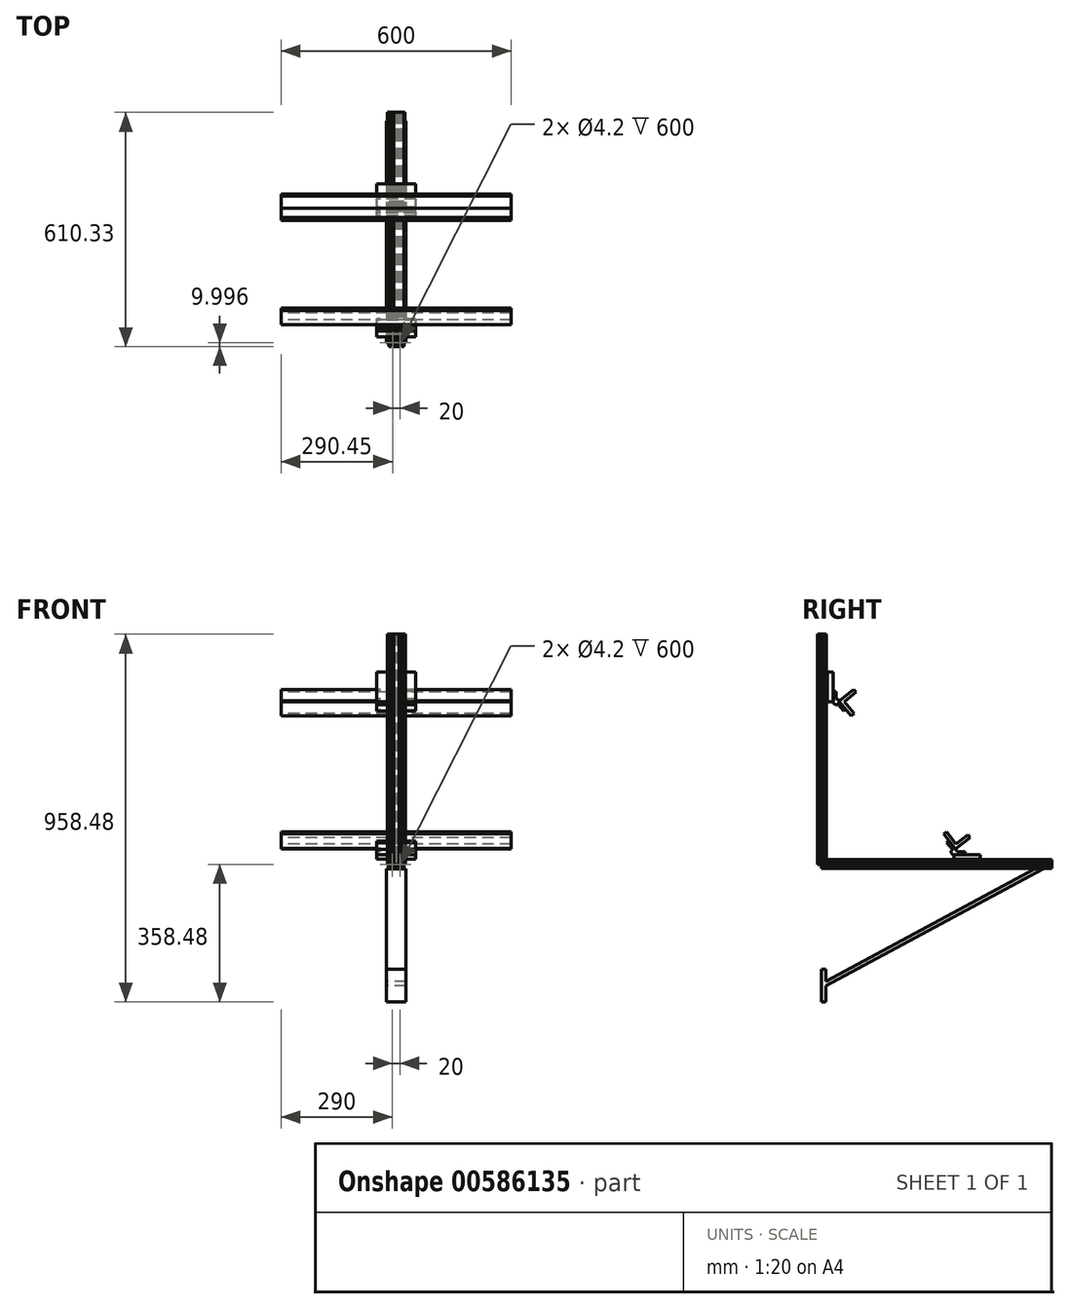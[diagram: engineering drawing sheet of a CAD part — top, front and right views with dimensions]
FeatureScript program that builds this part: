
annotation { "Feature Type Name" : "Feature", "Feature Type Description" : "" }
export const myFeature = defineFeature(function(context is Context, id is Id, definition is map)
    precondition{}
    {
        {
            var Q0;
            Q0=qCreatedBy(makeId("Front.planeOp"),FACE);
            var sketch = newSketch(context, id + "F0", { "sketchPlane" : qUnion([Q0])});
            skLineSegment(sketch, "E0.bottom", {"start": v(20, -10) * mm, "end": v(13, -10) * mm});
            skLineSegment(sketch, "E0.top", {"start": v(20, 10) * mm, "end": v(-7, 10) * mm});
            skLineSegment(sketch, "E0.left", {"start": v(20, -10) * mm, "end": v(20, -3) * mm});
            skLineSegment(sketch, "E0.right", {"start": v(-20, -10) * mm, "end": v(-20, -3) * mm});
            skPoint(sketch, "E0.middle", {"position": v(0, 0) * mm});
            skLineSegment(sketch, "E1.bottom", {"start": v(-8, -3) * mm, "end": v(-12, -3) * mm});
            skLineSegment(sketch, "E1.top", {"start": v(-8, 3) * mm, "end": v(-12, 3) * mm});
            skLineSegment(sketch, "E1.left", {"start": v(-7, -2) * mm, "end": v(-7, 2) * mm});
            skLineSegment(sketch, "E1.right", {"start": v(-13, -2) * mm, "end": v(-13, 2) * mm});
            skPoint(sketch, "E1.middle", {"position": v(-10, 0) * mm});
            skLineSegment(sketch, "E2.bottom", {"start": v(8, -3) * mm, "end": v(12, -3) * mm});
            skLineSegment(sketch, "E2.top", {"start": v(8, 3) * mm, "end": v(12, 3) * mm});
            skLineSegment(sketch, "E2.left", {"start": v(7, -2) * mm, "end": v(7, 2) * mm});
            skLineSegment(sketch, "E2.right", {"start": v(13, -2) * mm, "end": v(13, 2) * mm});
            skPoint(sketch, "E2.middle", {"position": v(10, 0) * mm});
            skLineSegment(sketch, "E3.bottom", {"start": v(-3, -8) * mm, "end": v(-7, -8) * mm});
            skLineSegment(sketch, "E3.top", {"start": v(-3, 8) * mm, "end": v(-7, 8) * mm});
            skLineSegment(sketch, "E3.right", {"start": v(-18, -6) * mm, "end": v(-18, -3) * mm});
            skLineSegment(sketch, "E4.bottom", {"start": v(3, -8) * mm, "end": v(7, -8) * mm});
            skLineSegment(sketch, "E4.top", {"start": v(3, 8) * mm, "end": v(16, 8) * mm});
            skLineSegment(sketch, "E5.bottom", {"start": v(-20, 10) * mm, "end": v(-16, 10) * mm});
            skLineSegment(sketch, "E5.top", {"start": v(-18, 6) * mm, "end": v(-17, 6) * mm});
            skLineSegment(sketch, "E5.right", {"start": v(-16, 8) * mm, "end": v(-16, 7) * mm});
            skPoint(sketch, "E5.middle", {"position": v(-18, 8) * mm});
            skLineSegment(sketch, "E6.bottom", {"start": v(-20, 10) * mm, "end": v(-19, 10) * mm});
            skLineSegment(sketch, "E7.top", {"start": v(-1, -10) * mm, "end": v(0, -10) * mm});
            skLineSegment(sketch, "E8", {"start": v(-16, 7) * mm, "end": v(-12, 3) * mm});
            skLineSegment(sketch, "E9", {"start": v(-3, -8) * mm, "end": v(-8, -3) * mm});
            skLineSegment(sketch, "E10.MirrorCS", {"start": v(-16, -7) * mm, "end": v(-12, -3) * mm});
            skLineSegment(sketch, "E11.MirrorCS", {"start": v(-3, 8) * mm, "end": v(-8, 3) * mm});
            skLineSegment(sketch, "E12.MirrorCS", {"start": v(3, 8) * mm, "end": v(8, 3) * mm});
            skLineSegment(sketch, "E13.MirrorCS", {"start": v(16, -7) * mm, "end": v(12, -3) * mm});
            skLineSegment(sketch, "E14.MirrorCS", {"start": v(16, 7) * mm, "end": v(12, 3) * mm});
            skLineSegment(sketch, "E15.MirrorCS", {"start": v(3, -8) * mm, "end": v(8, -3) * mm});
            skLineSegment(sketch, "E16.bottom", {"start": v(20, 10) * mm, "end": v(16, 10) * mm});
            skLineSegment(sketch, "E16.top", {"start": v(18, 6) * mm, "end": v(17, 6) * mm});
            skLineSegment(sketch, "E16.right", {"start": v(16, 8) * mm, "end": v(16, 7) * mm});
            skPoint(sketch, "E16.middle", {"position": v(18, 8) * mm});
            skLineSegment(sketch, "E17.bottom", {"start": v(20, -10) * mm, "end": v(16, -10) * mm});
            skLineSegment(sketch, "E17.top", {"start": v(18, -6) * mm, "end": v(17, -6) * mm});
            skLineSegment(sketch, "E17.left", {"start": v(20, -10) * mm, "end": v(20, -6) * mm});
            skLineSegment(sketch, "E17.right", {"start": v(16, -8) * mm, "end": v(16, -7) * mm});
            skPoint(sketch, "E17.middle", {"position": v(18, -8) * mm});
            skPoint(sketch, "E18.orphan", {"position": v(19, 10) * mm});
            skPoint(sketch, "E19.orphan", {"position": v(20, 9) * mm});
            skPoint(sketch, "E20.orphan", {"position": v(16, 6) * mm});
            skPoint(sketch, "E21.orphan", {"position": v(13, 3) * mm});
            skLineSegment(sketch, "E22.trimOffspring", {"start": v(13, -2) * mm, "end": v(17, -6) * mm});
            skLineSegment(sketch, "E23.trimOffspring", {"start": v(7, 2) * mm, "end": v(2, 7) * mm});
            skLineSegment(sketch, "E24.trimOffspring", {"start": v(7, -2) * mm, "end": v(2, -7) * mm});
            skLineSegment(sketch, "E25.trimOffspring", {"start": v(13, 2) * mm, "end": v(17, 6) * mm});
            skPoint(sketch, "E26.orphan", {"position": v(13, -3) * mm});
            skPoint(sketch, "E27.orphan", {"position": v(7, 3) * mm});
            skPoint(sketch, "E28.orphan", {"position": v(7, -3) * mm});
            skPoint(sketch, "E29.orphan", {"position": v(16, -6) * mm});
            skLineSegment(sketch, "E30.trimOffspring", {"start": v(18, -6) * mm, "end": v(18, -3) * mm});
            skPoint(sketch, "E31.trimOffspring.end.orphan", {"position": v(20, -9) * mm});
            skPoint(sketch, "E32.orphan", {"position": v(19, -10) * mm});
            skPoint(sketch, "E7.left.start.orphan", {"position": v(-1, -9) * mm});
            skPoint(sketch, "E33.orphan", {"position": v(-2, -8) * mm});
            skPoint(sketch, "E34.orphan", {"position": v(-18, -8) * mm});
            skPoint(sketch, "E35.orphan", {"position": v(-19, -10) * mm});
            skPoint(sketch, "E36.orphan", {"position": v(-20, -9) * mm});
            skPoint(sketch, "E37.orphan", {"position": v(-16, 6) * mm});
            skPoint(sketch, "E38.orphan", {"position": v(-1, 10) * mm});
            skPoint(sketch, "E39.orphan", {"position": v(0, 9) * mm});
            skPoint(sketch, "E40.orphan", {"position": v(1, 10) * mm});
            skPoint(sketch, "E41.orphan", {"position": v(2, 8) * mm});
            skPoint(sketch, "E42.orphan", {"position": v(-2, 8) * mm});
            skPoint(sketch, "E43.orphan", {"position": v(0, -9) * mm});
            skPoint(sketch, "E44.orphan", {"position": v(1, -10) * mm});
            skPoint(sketch, "E45.orphan", {"position": v(2, -8) * mm});
            skLineSegment(sketch, "E46", {"start": v(-1, -8) * mm, "end": v(1, -8) * mm});
            skLineSegment(sketch, "E47", {"start": v(1, 8) * mm, "end": v(-1, 8) * mm});
            skLineSegment(sketch, "E48", {"start": v(-2, 7) * mm, "end": v(-1, 8) * mm});
            skLineSegment(sketch, "E49", {"start": v(2, 7) * mm, "end": v(1, 8) * mm});
            skLineSegment(sketch, "E50", {"start": v(-2, -7) * mm, "end": v(-1, -8) * mm});
            skLineSegment(sketch, "E51", {"start": v(2, -7) * mm, "end": v(1, -8) * mm});
            skPoint(sketch, "E52.orphan", {"position": v(-13, 3) * mm});
            skPoint(sketch, "E53.orphan", {"position": v(-7, 3) * mm});
            skPoint(sketch, "E54.orphan", {"position": v(-7, -3) * mm});
            skPoint(sketch, "E55.orphan", {"position": v(-13, -3) * mm});
            skLineSegment(sketch, "E56.trimOffspring", {"start": v(-13, 2) * mm, "end": v(-17, 6) * mm});
            skLineSegment(sketch, "E57.trimOffspring", {"start": v(-7, -2) * mm, "end": v(-2, -7) * mm});
            skLineSegment(sketch, "E58.trimOffspring", {"start": v(-7, 2) * mm, "end": v(-2, 7) * mm});
            skLineSegment(sketch, "E59.trimOffspring", {"start": v(-13, -2) * mm, "end": v(-17, -6) * mm});
            skLineSegment(sketch, "E60.bottom", {"start": v(-20, -10) * mm, "end": v(-16, -10) * mm});
            skLineSegment(sketch, "E60.top", {"start": v(-18, -6) * mm, "end": v(-17, -6) * mm});
            skLineSegment(sketch, "E60.left", {"start": v(-20, -10) * mm, "end": v(-20, -6) * mm});
            skLineSegment(sketch, "E60.right", {"start": v(-16, -8) * mm, "end": v(-16, -7) * mm});
            skPoint(sketch, "E61.orphan", {"position": v(-16, -6) * mm});
            skLineSegment(sketch, "E62", {"start": v(-13, -8) * mm, "end": v(-13, -10) * mm});
            skLineSegment(sketch, "E63", {"start": v(-7, -8) * mm, "end": v(-7, -10) * mm});
            skLineSegment(sketch, "E64", {"start": v(-18, 3) * mm, "end": v(-20, 3) * mm});
            skLineSegment(sketch, "E65", {"start": v(-18, -3) * mm, "end": v(-20, -3) * mm});
            skLineSegment(sketch, "E66", {"start": v(-13, 8) * mm, "end": v(-13, 10) * mm});
            skLineSegment(sketch, "E67", {"start": v(-7, 8) * mm, "end": v(-7, 10) * mm});
            skLineSegment(sketch, "E68.MirrorCS", {"start": v(18, 3) * mm, "end": v(20, 3) * mm});
            skLineSegment(sketch, "E69.MirrorCS", {"start": v(18, -3) * mm, "end": v(20, -3) * mm});
            skLineSegment(sketch, "E70.MirrorCS", {"start": v(13, -8) * mm, "end": v(13, -10) * mm});
            skLineSegment(sketch, "E71.MirrorCS", {"start": v(7, -8) * mm, "end": v(7, -10) * mm});
            skLineSegment(sketch, "E72.trimOffspring", {"start": v(-18, 3) * mm, "end": v(-18, 6) * mm});
            skLineSegment(sketch, "E73.trimOffspring", {"start": v(-20, 3) * mm, "end": v(-20, 7.62) * mm});
            skLineSegment(sketch, "E74.trimOffspring", {"start": v(-13, 10) * mm, "end": v(-20, 10) * mm});
            skLineSegment(sketch, "E75.trimOffspring", {"start": v(-13, 8) * mm, "end": v(-16, 8) * mm});
            skLineSegment(sketch, "E76.trimOffspring", {"start": v(-13, -8) * mm, "end": v(-16, -8) * mm});
            skLineSegment(sketch, "E77.trimOffspring", {"start": v(-13, -10) * mm, "end": v(-20, -10) * mm});
            skLineSegment(sketch, "E78.trimOffspring", {"start": v(13, -8) * mm, "end": v(16, -8) * mm});
            skLineSegment(sketch, "E79.trimOffspring", {"start": v(7, -10) * mm, "end": v(-7, -10) * mm});
            skLineSegment(sketch, "E80.trimOffspring", {"start": v(20, 3) * mm, "end": v(20, 6) * mm});
            skLineSegment(sketch, "E81.trimOffspring", {"start": v(18, 3) * mm, "end": v(18, 6) * mm});
            skCircle(sketch, "E82", {"center": v(-10, 0) * mm, "radius": 2.1 * mm});
            skCircle(sketch, "E83.MirrorC", {"center": v(10, 0) * mm, "radius": 2.1 * mm});
            skLineSegment(sketch, "E84.top", {"start": v(20, 12.38) * mm, "end": v(20.44, 12.38) * mm});
            skLineSegment(sketch, "E84.left", {"start": v(20, 10) * mm, "end": v(20, 12.38) * mm});
            skLineSegment(sketch, "E85", {"start": v(20.44, 12.38) * mm, "end": v(23.18, 10) * mm});
            skLineSegment(sketch, "E86.MirrorCS", {"start": v(20.44, 7.62) * mm, "end": v(23.18, 10) * mm});
            skLineSegment(sketch, "E87.MirrorCS", {"start": v(20, 7.62) * mm, "end": v(20.44, 7.62) * mm});
            skLineSegment(sketch, "E88.MirrorCS", {"start": v(-20, 7.62) * mm, "end": v(-20.44, 7.62) * mm});
            skLineSegment(sketch, "E89.MirrorCS", {"start": v(-20.44, 7.62) * mm, "end": v(-23.18, 10) * mm});
            skLineSegment(sketch, "E90.MirrorCS", {"start": v(-20.44, 12.38) * mm, "end": v(-23.18, 10) * mm});
            skLineSegment(sketch, "E91.MirrorCS", {"start": v(-20, 12.38) * mm, "end": v(-20.44, 12.38) * mm});
            skLineSegment(sketch, "E92.MirrorCS", {"start": v(-20, 10) * mm, "end": v(-20, 12.38) * mm});
            skLineSegment(sketch, "E93.trimOffspring", {"start": v(-20, 7.62) * mm, "end": v(-20, 6) * mm});
            skPoint(sketch, "E94.trimOffspring.start.orphan", {"position": v(-20, 9) * mm});
            skLineSegment(sketch, "E95.trimOffspring", {"start": v(20, 7.62) * mm, "end": v(20, 6) * mm});
            skSolve(sketch);
        }
        {
            var Q0;
            Q0 = qSketchRegion(id + "F0", true);
            extrude(context, id + "F1", {"entities" : qUnion([Q0]), "oppositeDirection" : true, "depth" : 600 * mm, "offsetDistance" : 25.4 * mm});
        }
        {
            var Q0;
            Q0=qCreatedBy(makeId("Top.planeOp"),FACE);
            var sketch = newSketch(context, id + "F2", { "sketchPlane" : qUnion([Q0])});
            skLineSegment(sketch, "E96.bottom", {"start": v(20.45, -10.33) * mm, "end": v(13.45, -10.33) * mm});
            skLineSegment(sketch, "E96.top", {"start": v(20.45, 9.67) * mm, "end": v(-6.55, 9.67) * mm});
            skLineSegment(sketch, "E96.left", {"start": v(20.45, -10.33) * mm, "end": v(20.45, -3.33) * mm});
            skLineSegment(sketch, "E96.right", {"start": v(-19.55, -10.33) * mm, "end": v(-19.55, -3.33) * mm});
            skPoint(sketch, "E96.middle", {"position": v(0.45, -0.33) * mm});
            skLineSegment(sketch, "E97.bottom", {"start": v(-7.55, -3.33) * mm, "end": v(-11.55, -3.33) * mm});
            skLineSegment(sketch, "E97.top", {"start": v(-7.55, 2.67) * mm, "end": v(-11.55, 2.67) * mm});
            skLineSegment(sketch, "E97.left", {"start": v(-6.55, -2.33) * mm, "end": v(-6.55, 1.67) * mm});
            skLineSegment(sketch, "E97.right", {"start": v(-12.55, -2.33) * mm, "end": v(-12.55, 1.67) * mm});
            skPoint(sketch, "E97.middle", {"position": v(-9.55, -0.33) * mm});
            skLineSegment(sketch, "E98.bottom", {"start": v(8.45, -3.33) * mm, "end": v(12.45, -3.33) * mm});
            skLineSegment(sketch, "E98.top", {"start": v(8.45, 2.67) * mm, "end": v(12.45, 2.67) * mm});
            skLineSegment(sketch, "E98.left", {"start": v(7.45, -2.33) * mm, "end": v(7.45, 1.67) * mm});
            skLineSegment(sketch, "E98.right", {"start": v(13.45, -2.33) * mm, "end": v(13.45, 1.67) * mm});
            skPoint(sketch, "E98.middle", {"position": v(10.45, -0.33) * mm});
            skLineSegment(sketch, "E99.bottom", {"start": v(-2.55, -8.33) * mm, "end": v(-6.55, -8.33) * mm});
            skLineSegment(sketch, "E99.top", {"start": v(-2.55, 7.67) * mm, "end": v(-6.55, 7.67) * mm});
            skLineSegment(sketch, "E99.right", {"start": v(-17.55, -6.33) * mm, "end": v(-17.55, -3.33) * mm});
            skLineSegment(sketch, "E100.bottom", {"start": v(3.45, -8.33) * mm, "end": v(7.45, -8.33) * mm});
            skLineSegment(sketch, "E100.top", {"start": v(3.45, 7.67) * mm, "end": v(16.45, 7.67) * mm});
            skLineSegment(sketch, "E101.bottom", {"start": v(-19.55, 9.67) * mm, "end": v(-15.55, 9.67) * mm});
            skLineSegment(sketch, "E101.top", {"start": v(-17.55, 5.67) * mm, "end": v(-16.55, 5.67) * mm});
            skLineSegment(sketch, "E101.right", {"start": v(-15.55, 7.67) * mm, "end": v(-15.55, 6.67) * mm});
            skPoint(sketch, "E101.middle", {"position": v(-17.55, 7.67) * mm});
            skLineSegment(sketch, "E102.bottom", {"start": v(-19.55, 9.67) * mm, "end": v(-18.55, 9.67) * mm});
            skLineSegment(sketch, "E103.top", {"start": v(-0.55, -10.33) * mm, "end": v(0.45, -10.33) * mm});
            skLineSegment(sketch, "E104", {"start": v(-15.55, 6.67) * mm, "end": v(-11.55, 2.67) * mm});
            skLineSegment(sketch, "E105", {"start": v(-2.55, -8.33) * mm, "end": v(-7.55, -3.33) * mm});
            skLineSegment(sketch, "E106.MirrorCS", {"start": v(-15.55, -7.33) * mm, "end": v(-11.55, -3.33) * mm});
            skLineSegment(sketch, "E107.MirrorCS", {"start": v(-2.55, 7.67) * mm, "end": v(-7.55, 2.67) * mm});
            skLineSegment(sketch, "E108.MirrorCS", {"start": v(3.45, 7.67) * mm, "end": v(8.45, 2.67) * mm});
            skLineSegment(sketch, "E109.MirrorCS", {"start": v(16.45, -7.33) * mm, "end": v(12.45, -3.33) * mm});
            skLineSegment(sketch, "E110.MirrorCS", {"start": v(16.45, 6.67) * mm, "end": v(12.45, 2.67) * mm});
            skLineSegment(sketch, "E111.MirrorCS", {"start": v(3.45, -8.33) * mm, "end": v(8.45, -3.33) * mm});
            skLineSegment(sketch, "E112.bottom", {"start": v(20.45, 9.67) * mm, "end": v(16.45, 9.67) * mm});
            skLineSegment(sketch, "E112.top", {"start": v(18.45, 5.67) * mm, "end": v(17.45, 5.67) * mm});
            skLineSegment(sketch, "E112.right", {"start": v(16.45, 7.67) * mm, "end": v(16.45, 6.67) * mm});
            skPoint(sketch, "E112.middle", {"position": v(18.45, 7.67) * mm});
            skLineSegment(sketch, "E113.bottom", {"start": v(20.45, -10.33) * mm, "end": v(16.45, -10.33) * mm});
            skLineSegment(sketch, "E113.top", {"start": v(18.45, -6.33) * mm, "end": v(17.45, -6.33) * mm});
            skLineSegment(sketch, "E113.left", {"start": v(20.45, -10.33) * mm, "end": v(20.45, -6.33) * mm});
            skLineSegment(sketch, "E113.right", {"start": v(16.45, -8.33) * mm, "end": v(16.45, -7.33) * mm});
            skPoint(sketch, "E113.middle", {"position": v(18.45, -8.33) * mm});
            skPoint(sketch, "E114.orphan", {"position": v(19.45, 9.67) * mm});
            skPoint(sketch, "E115.orphan", {"position": v(20.45, 8.67) * mm});
            skPoint(sketch, "E116.orphan", {"position": v(16.45, 5.67) * mm});
            skPoint(sketch, "E117.orphan", {"position": v(13.45, 2.67) * mm});
            skLineSegment(sketch, "E118.trimOffspring", {"start": v(13.45, -2.33) * mm, "end": v(17.45, -6.33) * mm});
            skLineSegment(sketch, "E119.trimOffspring", {"start": v(7.45, 1.67) * mm, "end": v(2.45, 6.67) * mm});
            skLineSegment(sketch, "E120.trimOffspring", {"start": v(7.45, -2.33) * mm, "end": v(2.45, -7.33) * mm});
            skLineSegment(sketch, "E121.trimOffspring", {"start": v(13.45, 1.67) * mm, "end": v(17.45, 5.67) * mm});
            skPoint(sketch, "E122.orphan", {"position": v(13.45, -3.33) * mm});
            skPoint(sketch, "E123.orphan", {"position": v(7.45, 2.67) * mm});
            skPoint(sketch, "E124.orphan", {"position": v(7.45, -3.33) * mm});
            skPoint(sketch, "E125.orphan", {"position": v(16.45, -6.33) * mm});
            skLineSegment(sketch, "E126.trimOffspring", {"start": v(18.45, -6.33) * mm, "end": v(18.45, -3.33) * mm});
            skPoint(sketch, "E127.trimOffspring.end.orphan", {"position": v(20.45, -9.33) * mm});
            skPoint(sketch, "E128.orphan", {"position": v(19.45, -10.33) * mm});
            skPoint(sketch, "E103.left.start.orphan", {"position": v(-0.55, -9.33) * mm});
            skPoint(sketch, "E129.orphan", {"position": v(-1.55, -8.33) * mm});
            skPoint(sketch, "E130.orphan", {"position": v(-17.55, -8.33) * mm});
            skPoint(sketch, "E131.orphan", {"position": v(-18.55, -10.33) * mm});
            skPoint(sketch, "E132.orphan", {"position": v(-19.55, -9.33) * mm});
            skPoint(sketch, "E133.orphan", {"position": v(-15.55, 5.67) * mm});
            skPoint(sketch, "E134.orphan", {"position": v(-0.55, 9.67) * mm});
            skPoint(sketch, "E135.orphan", {"position": v(0.45, 8.67) * mm});
            skPoint(sketch, "E136.orphan", {"position": v(1.45, 9.67) * mm});
            skPoint(sketch, "E137.orphan", {"position": v(2.45, 7.67) * mm});
            skPoint(sketch, "E138.orphan", {"position": v(-1.55, 7.67) * mm});
            skPoint(sketch, "E139.orphan", {"position": v(0.45, -9.33) * mm});
            skPoint(sketch, "E140.orphan", {"position": v(1.45, -10.33) * mm});
            skPoint(sketch, "E141.orphan", {"position": v(2.45, -8.33) * mm});
            skLineSegment(sketch, "E142", {"start": v(-0.55, -8.33) * mm, "end": v(1.45, -8.33) * mm});
            skLineSegment(sketch, "E143", {"start": v(1.45, 7.67) * mm, "end": v(-0.55, 7.67) * mm});
            skLineSegment(sketch, "E144", {"start": v(-1.55, 6.67) * mm, "end": v(-0.55, 7.67) * mm});
            skLineSegment(sketch, "E145", {"start": v(2.45, 6.67) * mm, "end": v(1.45, 7.67) * mm});
            skLineSegment(sketch, "E146", {"start": v(-1.55, -7.33) * mm, "end": v(-0.55, -8.33) * mm});
            skLineSegment(sketch, "E147", {"start": v(2.45, -7.33) * mm, "end": v(1.45, -8.33) * mm});
            skPoint(sketch, "E148.orphan", {"position": v(-12.55, 2.67) * mm});
            skPoint(sketch, "E149.orphan", {"position": v(-6.55, 2.67) * mm});
            skPoint(sketch, "E150.orphan", {"position": v(-6.55, -3.33) * mm});
            skPoint(sketch, "E151.orphan", {"position": v(-12.55, -3.33) * mm});
            skLineSegment(sketch, "E152.trimOffspring", {"start": v(-12.55, 1.67) * mm, "end": v(-16.55, 5.67) * mm});
            skLineSegment(sketch, "E153.trimOffspring", {"start": v(-6.55, -2.33) * mm, "end": v(-1.55, -7.33) * mm});
            skLineSegment(sketch, "E154.trimOffspring", {"start": v(-6.55, 1.67) * mm, "end": v(-1.55, 6.67) * mm});
            skLineSegment(sketch, "E155.trimOffspring", {"start": v(-12.55, -2.33) * mm, "end": v(-16.55, -6.33) * mm});
            skLineSegment(sketch, "E156.bottom", {"start": v(-19.55, -10.33) * mm, "end": v(-15.55, -10.33) * mm});
            skLineSegment(sketch, "E156.top", {"start": v(-17.55, -6.33) * mm, "end": v(-16.55, -6.33) * mm});
            skLineSegment(sketch, "E156.left", {"start": v(-19.55, -10.33) * mm, "end": v(-19.55, -6.33) * mm});
            skLineSegment(sketch, "E156.right", {"start": v(-15.55, -8.33) * mm, "end": v(-15.55, -7.33) * mm});
            skPoint(sketch, "E157.orphan", {"position": v(-15.55, -6.33) * mm});
            skLineSegment(sketch, "E158", {"start": v(-12.55, -8.33) * mm, "end": v(-12.55, -10.33) * mm});
            skLineSegment(sketch, "E159", {"start": v(-6.55, -8.33) * mm, "end": v(-6.55, -10.33) * mm});
            skLineSegment(sketch, "E160", {"start": v(-17.55, 2.67) * mm, "end": v(-19.55, 2.67) * mm});
            skLineSegment(sketch, "E161", {"start": v(-17.55, -3.33) * mm, "end": v(-19.55, -3.33) * mm});
            skLineSegment(sketch, "E162", {"start": v(-12.55, 7.67) * mm, "end": v(-12.55, 9.67) * mm});
            skLineSegment(sketch, "E163", {"start": v(-6.55, 7.67) * mm, "end": v(-6.55, 9.67) * mm});
            skLineSegment(sketch, "E164.MirrorCS", {"start": v(18.45, 2.67) * mm, "end": v(20.45, 2.67) * mm});
            skLineSegment(sketch, "E165.MirrorCS", {"start": v(18.45, -3.33) * mm, "end": v(20.45, -3.33) * mm});
            skLineSegment(sketch, "E166.MirrorCS", {"start": v(13.45, -8.33) * mm, "end": v(13.45, -10.33) * mm});
            skLineSegment(sketch, "E167.MirrorCS", {"start": v(7.45, -8.33) * mm, "end": v(7.45, -10.33) * mm});
            skLineSegment(sketch, "E168.trimOffspring", {"start": v(-17.55, 2.67) * mm, "end": v(-17.55, 5.67) * mm});
            skLineSegment(sketch, "E169.trimOffspring", {"start": v(-19.55, 2.67) * mm, "end": v(-19.55, 7.29) * mm});
            skLineSegment(sketch, "E170.trimOffspring", {"start": v(-12.55, 9.67) * mm, "end": v(-19.55, 9.67) * mm});
            skLineSegment(sketch, "E171.trimOffspring", {"start": v(-12.55, 7.67) * mm, "end": v(-15.55, 7.67) * mm});
            skLineSegment(sketch, "E172.trimOffspring", {"start": v(-12.55, -8.33) * mm, "end": v(-15.55, -8.33) * mm});
            skLineSegment(sketch, "E173.trimOffspring", {"start": v(-12.55, -10.33) * mm, "end": v(-19.55, -10.33) * mm});
            skLineSegment(sketch, "E174.trimOffspring", {"start": v(13.45, -8.33) * mm, "end": v(16.45, -8.33) * mm});
            skLineSegment(sketch, "E175.trimOffspring", {"start": v(7.45, -10.33) * mm, "end": v(-6.55, -10.33) * mm});
            skLineSegment(sketch, "E176.trimOffspring", {"start": v(20.45, 2.67) * mm, "end": v(20.45, 5.67) * mm});
            skLineSegment(sketch, "E177.trimOffspring", {"start": v(18.45, 2.67) * mm, "end": v(18.45, 5.67) * mm});
            skCircle(sketch, "E178", {"center": v(-9.55, -0.33) * mm, "radius": 2.1 * mm});
            skCircle(sketch, "E179.MirrorC", {"center": v(10.45, -0.33) * mm, "radius": 2.1 * mm});
            skLineSegment(sketch, "E180.top", {"start": v(20.45, 12.05) * mm, "end": v(20.9, 12.05) * mm});
            skLineSegment(sketch, "E180.left", {"start": v(20.45, 9.67) * mm, "end": v(20.45, 12.05) * mm});
            skLineSegment(sketch, "E181", {"start": v(20.9, 12.05) * mm, "end": v(23.63, 9.67) * mm});
            skLineSegment(sketch, "E182.MirrorCS", {"start": v(20.9, 7.29) * mm, "end": v(23.63, 9.67) * mm});
            skLineSegment(sketch, "E183.MirrorCS", {"start": v(20.45, 7.29) * mm, "end": v(20.9, 7.29) * mm});
            skLineSegment(sketch, "E184.MirrorCS", {"start": v(-19.55, 7.29) * mm, "end": v(-20, 7.29) * mm});
            skLineSegment(sketch, "E185.MirrorCS", {"start": v(-20, 7.29) * mm, "end": v(-22.73, 9.67) * mm});
            skLineSegment(sketch, "E186.MirrorCS", {"start": v(-20, 12.05) * mm, "end": v(-22.73, 9.67) * mm});
            skLineSegment(sketch, "E187.MirrorCS", {"start": v(-19.55, 12.05) * mm, "end": v(-20, 12.05) * mm});
            skLineSegment(sketch, "E188.MirrorCS", {"start": v(-19.55, 9.67) * mm, "end": v(-19.55, 12.05) * mm});
            skLineSegment(sketch, "E189.trimOffspring", {"start": v(-19.55, 7.29) * mm, "end": v(-19.55, 5.67) * mm});
            skPoint(sketch, "E190.trimOffspring.start.orphan", {"position": v(-19.55, 8.67) * mm});
            skLineSegment(sketch, "E191.trimOffspring", {"start": v(20.45, 7.29) * mm, "end": v(20.45, 5.67) * mm});
            skSolve(sketch);
        }
        {
            var Q0;
            Q0 = qSketchRegion(id + "F2", true);
            extrude(context, id + "F3", {"entities" : qUnion([Q0]), "operationType" : NewBodyOperationType.ADD, "depth" : 600 * mm, "offsetDistance" : 25.4 * mm});
        }
        {
            var Q0;
            Q0=qCreatedBy(makeId("Right.planeOp"),FACE);
            var sketch = newSketch(context, id + "F4", { "sketchPlane" : qUnion([Q0])});
            skLineSegment(sketch, "E192.right", {"start": v(577.1, -11.57) * mm, "end": v(577.1, -11.74) * mm});
            skLineSegment(sketch, "E193", {"start": v(555.61, -11.57) * mm, "end": v(11.28, -304.62) * mm});
            skLineSegment(sketch, "E194", {"start": v(577.42, -11.57) * mm, "end": v(11.28, -316.37) * mm});
            skLineSegment(sketch, "E195", {"start": v(0, -322.44) * mm, "end": v(0, -310.7) * mm});
            skLineSegment(sketch, "E196", {"start": v(555.61, -11.57) * mm, "end": v(577.42, -11.57) * mm});
            skPoint(sketch, "E197.orphan", {"position": v(577.1, 0) * mm});
            skPoint(sketch, "E198.orphan", {"position": v(598.9, 0) * mm});
            skLineSegment(sketch, "E199.top", {"start": v(0, -358.48) * mm, "end": v(11.28, -358.48) * mm});
            skLineSegment(sketch, "E199.left", {"start": v(0, -291.08) * mm, "end": v(0, -358.48) * mm});
            skLineSegment(sketch, "E199.right", {"start": v(11.28, -291.08) * mm, "end": v(11.28, -304.62) * mm});
            skLineSegment(sketch, "E200.top", {"start": v(11.28, -272.73) * mm, "end": v(0, -272.73) * mm});
            skLineSegment(sketch, "E200.left", {"start": v(11.28, -291.08) * mm, "end": v(11.28, -272.73) * mm});
            skLineSegment(sketch, "E200.right", {"start": v(0, -291.08) * mm, "end": v(0, -272.73) * mm});
            skLineSegment(sketch, "E201.trimOffspring", {"start": v(11.28, -316.37) * mm, "end": v(11.28, -358.48) * mm});
            skSolve(sketch);
        }
        {
            var Q0;
            Q0 = qSketchRegion(id + "F4", true);
            extrude(context, id + "F5", {"entities" : qUnion([Q0]), "depth" : 25.4 * mm, "offsetDistance" : 25.4 * mm, "hasSecondDirection" : true, "secondDirectionOppositeDirection" : true, "secondDirectionDepth" : 25.4 * mm});
        }
        {
            var Q0;
            Q0=qCreatedBy(makeId("Right.planeOp"),FACE);
            var sketch = newSketch(context, id + "F6", { "sketchPlane" : qUnion([Q0])});
            skLineSegment(sketch, "E202", {"start": v(31.2, 420.16) * mm, "end": v(339.93, 26.86) * mm});
            skLineSegment(sketch, "E203.bottom", {"start": v(345.64, 13.63) * mm, "end": v(413.27, 13.63) * mm});
            skLineSegment(sketch, "E203.top", {"start": v(345.64, 25.03) * mm, "end": v(413.27, 25.03) * mm});
            skLineSegment(sketch, "E203.left", {"start": v(345.64, 13.63) * mm, "end": v(345.64, 25.03) * mm});
            skLineSegment(sketch, "E203.right", {"start": v(413.27, 13.63) * mm, "end": v(413.27, 25.03) * mm});
            skCircle(sketch, "E204", {"center": v(345.64, 32.7) * mm, "radius": 7.67 * mm});
            skLineSegment(sketch, "E205", {"start": v(345.64, 32.7) * mm, "end": v(326.32, 57.32) * mm});
            skLineSegment(sketch, "E206", {"start": v(326.32, 57.32) * mm, "end": v(330.53, 60.62) * mm});
            skLineSegment(sketch, "E207", {"start": v(330.53, 60.62) * mm, "end": v(346.46, 40.32) * mm});
            skLineSegment(sketch, "E208", {"start": v(185.56, 223.5) * mm, "end": v(222.86, 252.78) * mm});
            skLineSegment(sketch, "E209.MirrorCS", {"start": v(38.23, 424.32) * mm, "end": v(57.55, 399.7) * mm});
            skLineSegment(sketch, "E210.MirrorCS", {"start": v(57.55, 399.7) * mm, "end": v(61.76, 403.01) * mm});
            skLineSegment(sketch, "E211.MirrorCS", {"start": v(61.76, 403.01) * mm, "end": v(45.83, 423.3) * mm});
            skCircle(sketch, "E212.MirrorC", {"center": v(38.23, 424.32) * mm, "radius": 7.67 * mm});
            skLineSegment(sketch, "E213.bottom", {"start": v(30.56, 424.32) * mm, "end": v(15.48, 424.32) * mm});
            skLineSegment(sketch, "E213.top", {"start": v(30.56, 502) * mm, "end": v(15.48, 502) * mm});
            skLineSegment(sketch, "E213.left", {"start": v(30.56, 424.32) * mm, "end": v(30.56, 502) * mm});
            skLineSegment(sketch, "E213.right", {"start": v(15.48, 424.32) * mm, "end": v(15.48, 502) * mm});
            skLineSegment(sketch, "E214.bottom", {"start": v(38.23, 424.32) * mm, "end": v(38.23, 424.32) * mm});
            skLineSegment(sketch, "E214.top", {"start": v(38.23, 451.2) * mm, "end": v(38.23, 451.2) * mm});
            skLineSegment(sketch, "E214.left", {"start": v(38.23, 424.32) * mm, "end": v(38.23, 451.2) * mm});
            skLineSegment(sketch, "E214.right", {"start": v(38.23, 424.32) * mm, "end": v(38.23, 451.2) * mm});
            skLineSegment(sketch, "E215.right", {"start": v(30.56, 451.2) * mm, "end": v(30.56, 451.2) * mm});
            skLineSegment(sketch, "E216", {"start": v(345.64, 32.7) * mm, "end": v(374.18, 32.7) * mm});
            skLineSegment(sketch, "E217.bottom", {"start": v(38.23, 451.2) * mm, "end": v(30.95, 451.2) * mm});
            skLineSegment(sketch, "E217.top", {"start": v(38.23, 426.74) * mm, "end": v(30.95, 426.74) * mm});
            skLineSegment(sketch, "E217.left", {"start": v(38.23, 451.2) * mm, "end": v(38.23, 426.74) * mm});
            skLineSegment(sketch, "E217.right", {"start": v(30.95, 451.2) * mm, "end": v(30.95, 426.74) * mm});
            skLineSegment(sketch, "E218.bottom", {"start": v(374.18, 32.7) * mm, "end": v(347.68, 32.7) * mm});
            skLineSegment(sketch, "E218.top", {"start": v(374.18, 25.3) * mm, "end": v(347.68, 25.3) * mm});
            skLineSegment(sketch, "E218.left", {"start": v(374.18, 32.7) * mm, "end": v(374.18, 25.3) * mm});
            skLineSegment(sketch, "E218.right", {"start": v(347.68, 32.7) * mm, "end": v(347.68, 25.3) * mm});
            skSolve(sketch);
        }
        {
            var Q0;
            Q0 = qSketchRegion(id + "F6", true);
            extrude(context, id + "F7", {"entities" : qUnion([Q0]), "depth" : 50.8 * mm, "offsetDistance" : 25.4 * mm, "hasSecondDirection" : true, "secondDirectionOppositeDirection" : true, "secondDirectionDepth" : 50.8 * mm});
        }
        {
            var Q0;
            Q0=qCreatedBy(makeId("Right.planeOp"),FACE);
            var sketch = newSketch(context, id + "F8", { "sketchPlane" : qUnion([Q0])});
            skLineSegment(sketch, "E219", {"start": v(46.93, 424.2) * mm, "end": v(77.13, 387.33) * mm});
            skLineSegment(sketch, "E220", {"start": v(77.13, 387.33) * mm, "end": v(84.4, 393.3) * mm});
            skLineSegment(sketch, "E221", {"start": v(84.4, 393.3) * mm, "end": v(59.18, 424.09) * mm});
            skLineSegment(sketch, "E222", {"start": v(59.18, 424.09) * mm, "end": v(89.67, 449.06) * mm});
            skLineSegment(sketch, "E223", {"start": v(89.67, 449.06) * mm, "end": v(83.8, 456.22) * mm});
            skLineSegment(sketch, "E224", {"start": v(83.8, 456.22) * mm, "end": v(46.93, 426.01) * mm});
            skLineSegment(sketch, "E225", {"start": v(46.93, 426.01) * mm, "end": v(46.93, 424.2) * mm});
            skLineSegment(sketch, "E226.MirrorCS", {"start": v(349.35, 40.75) * mm, "end": v(347.59, 41.18) * mm});
            skLineSegment(sketch, "E227.MirrorCS", {"start": v(387.45, 69.4) * mm, "end": v(349.35, 40.75) * mm});
            skLineSegment(sketch, "E228.MirrorCS", {"start": v(350.4, 53.1) * mm, "end": v(381.9, 76.8) * mm});
            skLineSegment(sketch, "E229.MirrorCS", {"start": v(326.47, 84.93) * mm, "end": v(350.4, 53.1) * mm});
            skLineSegment(sketch, "E230.MirrorCS", {"start": v(347.59, 41.18) * mm, "end": v(318.95, 79.27) * mm});
            skLineSegment(sketch, "E231.MirrorCS", {"start": v(381.9, 76.8) * mm, "end": v(387.45, 69.4) * mm});
            skLineSegment(sketch, "E232.MirrorCS", {"start": v(318.95, 79.27) * mm, "end": v(326.47, 84.93) * mm});
            skSolve(sketch);
        }
        {
            var Q0;
            Q0 = qSketchRegion(id + "F8", true);
            extrude(context, id + "F9", {"entities" : qUnion([Q0]), "depth" : 300 * mm, "offsetDistance" : 25.4 * mm, "hasSecondDirection" : true, "secondDirectionOppositeDirection" : true, "secondDirectionDepth" : 300 * mm});
        }
    });
